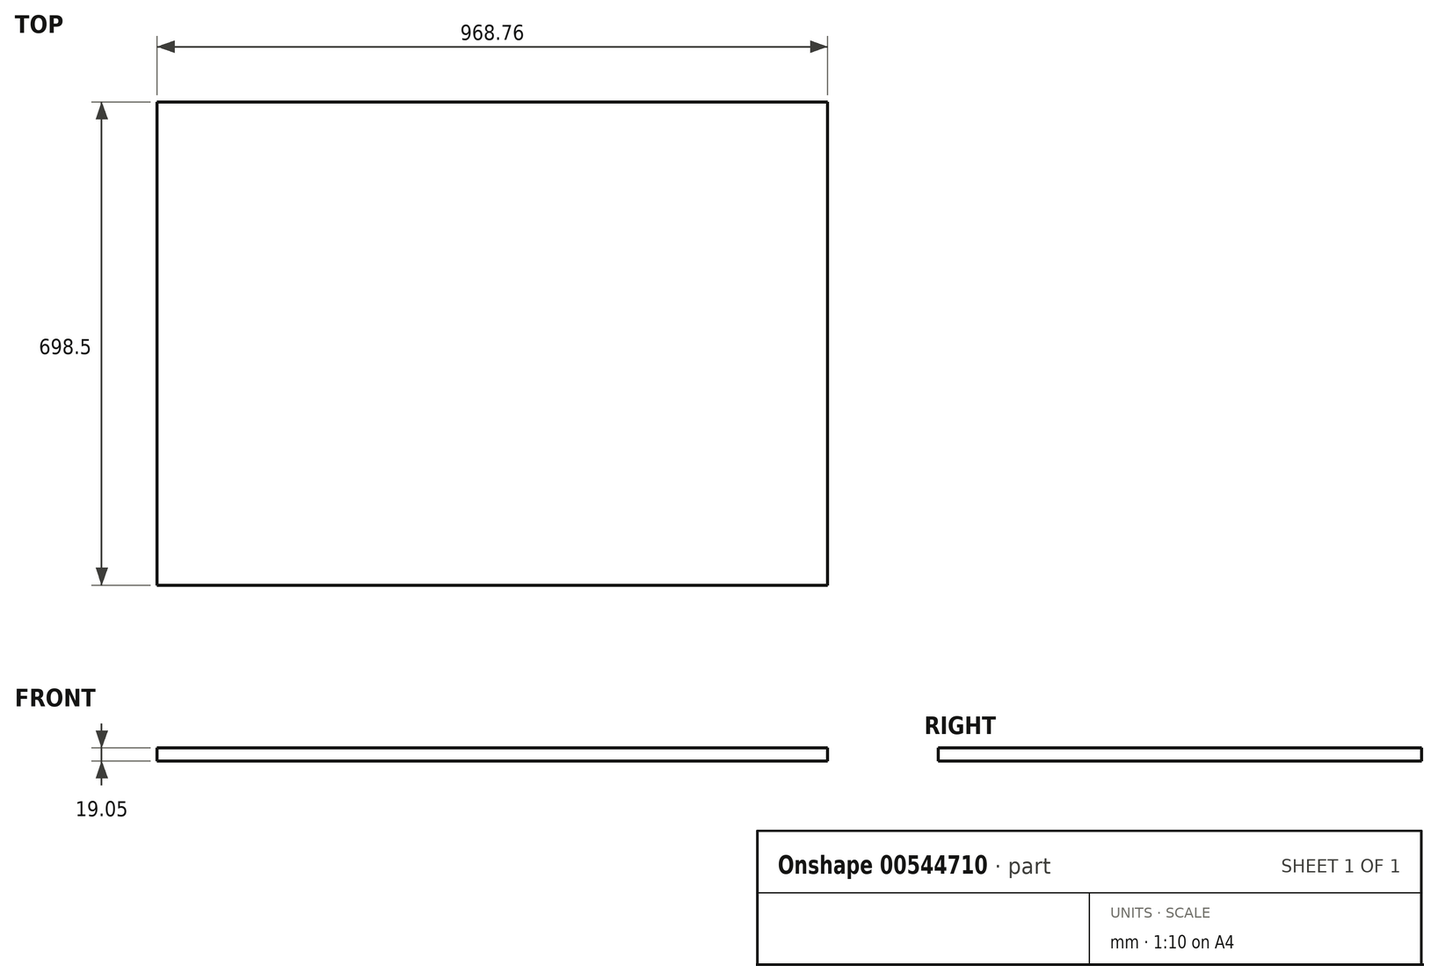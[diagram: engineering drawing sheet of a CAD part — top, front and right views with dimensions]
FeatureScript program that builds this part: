
annotation { "Feature Type Name" : "Feature", "Feature Type Description" : "" }
export const myFeature = defineFeature(function(context is Context, id is Id, definition is map)
    precondition{}
    {
        {
            var Q0;
            Q0=qCreatedBy(makeId("Top.planeOp"),FACE);
            var sketch = newSketch(context, id + "F0", { "sketchPlane" : qUnion([Q0])});
            skLineSegment(sketch, "E0.bottom", {"start": v(0, 0) * mm, "end": v(968.76, 0) * mm});
            skLineSegment(sketch, "E0.top", {"start": v(0, 698.5) * mm, "end": v(968.76, 698.5) * mm});
            skLineSegment(sketch, "E0.left", {"start": v(0, 0) * mm, "end": v(0, 698.5) * mm});
            skLineSegment(sketch, "E0.right", {"start": v(968.76, 0) * mm, "end": v(968.76, 698.5) * mm});
            skSolve(sketch);
        }
        {
            var Q0;
            Q0=makeQuery(id+"F0.imprint","IMPRINT",FACE,{"disambiguationData":[TD([[makeQuery(id+"F0.imprint","IMPRINT",EDGE,{"derivedFrom":sQuery(id+"F0.wireOp",EDGE,"E0.bottom")}),1.0]])]});
            extrude(context, id + "F1", {"entities" : qUnion([Q0]), "depth" : 19.05 * mm, "offsetDistance" : 25.4 * mm});
        }
    });
